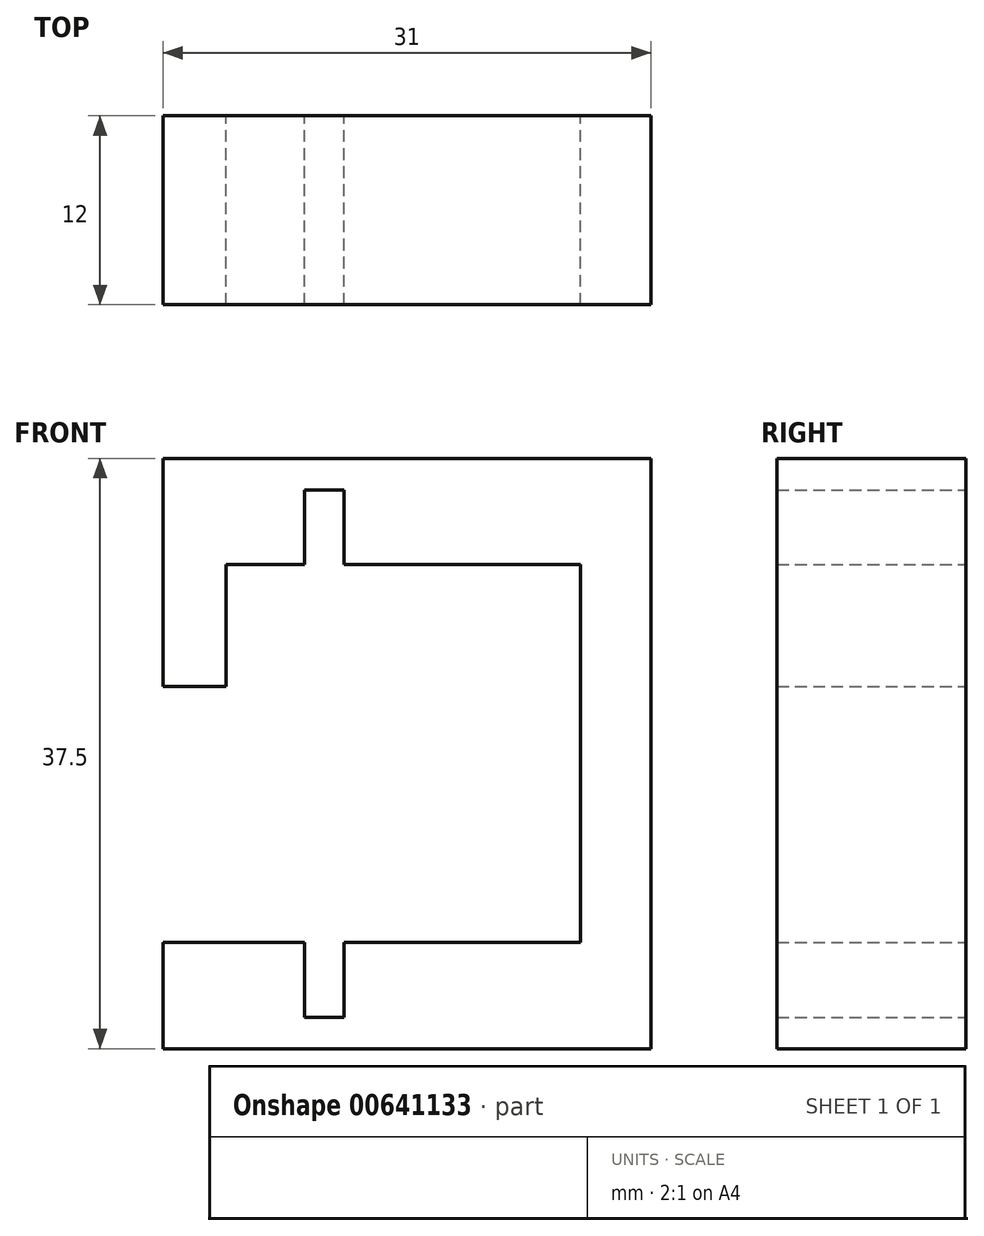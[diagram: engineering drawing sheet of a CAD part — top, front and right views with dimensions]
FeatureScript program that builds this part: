
annotation { "Feature Type Name" : "Feature", "Feature Type Description" : "" }
export const myFeature = defineFeature(function(context is Context, id is Id, definition is map)
    precondition{}
    {
        {
            var Q0;
            Q0=qCreatedBy(makeId("Front.planeOp"),FACE);
            var sketch = newSketch(context, id + "F0", { "sketchPlane" : qUnion([Q0])});
            skLineSegment(sketch, "E0", {"start": v(0, 16.75) * mm, "end": v(2.5, 16.75) * mm});
            skLineSegment(sketch, "E1", {"start": v(2.5, 16.75) * mm, "end": v(2.5, 12) * mm});
            skLineSegment(sketch, "E2", {"start": v(2.5, 12) * mm, "end": v(17.5, 12) * mm});
            skLineSegment(sketch, "E3", {"start": v(17.5, 12) * mm, "end": v(17.5, -12) * mm});
            skLineSegment(sketch, "E4", {"start": v(17.5, -12) * mm, "end": v(2.5, -12) * mm});
            skLineSegment(sketch, "E5", {"start": v(2.5, -12) * mm, "end": v(2.5, -16.75) * mm});
            skLineSegment(sketch, "E6", {"start": v(2.5, -16.75) * mm, "end": v(0, -16.75) * mm});
            skLineSegment(sketch, "E7", {"start": v(0, -16.75) * mm, "end": v(0, -12) * mm});
            skLineSegment(sketch, "E8", {"start": v(0, -12) * mm, "end": v(-9, -12) * mm});
            skLineSegment(sketch, "E9", {"start": v(-9, -12) * mm, "end": v(-9, -18.75) * mm});
            skLineSegment(sketch, "E10", {"start": v(-9, -18.75) * mm, "end": v(22, -18.75) * mm});
            skLineSegment(sketch, "E11", {"start": v(22, -18.75) * mm, "end": v(22, 18.75) * mm});
            skLineSegment(sketch, "E12", {"start": v(22, 18.75) * mm, "end": v(-9, 18.75) * mm});
            skLineSegment(sketch, "E13", {"start": v(-9, 4.25) * mm, "end": v(-9, 18.75) * mm});
            skLineSegment(sketch, "E14", {"start": v(0, 16.75) * mm, "end": v(0, 12) * mm});
            skLineSegment(sketch, "E15", {"start": v(0, 12) * mm, "end": v(-5, 12) * mm});
            skLineSegment(sketch, "E16", {"start": v(-5, 12) * mm, "end": v(-5, 4.25) * mm});
            skLineSegment(sketch, "E17", {"start": v(-5, 4.25) * mm, "end": v(-9, 4.25) * mm});
            skSolve(sketch);
        }
        {
            var Q0;
            Q0 = qSketchRegion(id + "F0", true);
            extrude(context, id + "F1", {"entities" : qUnion([Q0]), "depth" : 12 * mm, "offsetDistance" : 25 * mm});
        }
    });
